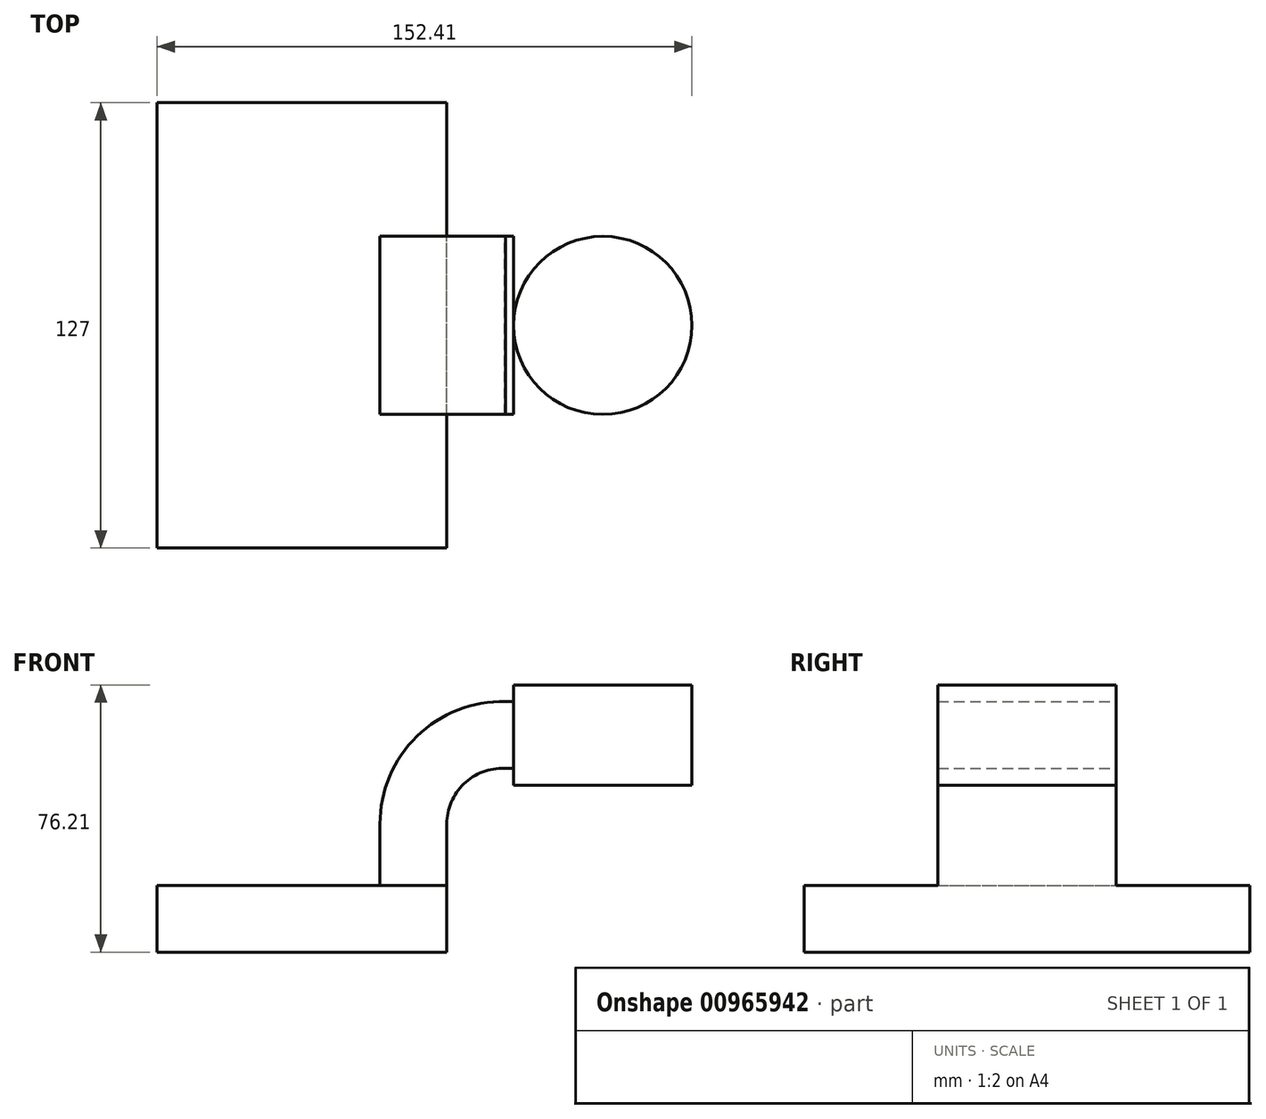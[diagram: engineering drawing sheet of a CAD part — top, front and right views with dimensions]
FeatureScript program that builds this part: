
annotation { "Feature Type Name" : "Feature", "Feature Type Description" : "" }
export const myFeature = defineFeature(function(context is Context, id is Id, definition is map)
    precondition{}
    {
        {
            var Q0;
            Q0=qCreatedBy(makeId("Front.planeOp"),FACE);
            var sketch = newSketch(context, id + "F0", { "sketchPlane" : qUnion([Q0])});
            skLineSegment(sketch, "E0.bottom", {"start": v(-41.28, 9.52) * mm, "end": v(41.28, 9.53) * mm});
            skLineSegment(sketch, "E0.top", {"start": v(-41.28, -9.53) * mm, "end": v(41.28, -9.53) * mm});
            skLineSegment(sketch, "E0.left", {"start": v(-41.28, 9.52) * mm, "end": v(-41.27, -9.53) * mm});
            skLineSegment(sketch, "E0.right", {"start": v(41.28, 9.53) * mm, "end": v(41.28, -9.52) * mm});
            skPoint(sketch, "E0.middle", {"position": v(0, 0) * mm});
            skLineSegment(sketch, "E1.bottom", {"start": v(60.32, 66.67) * mm, "end": v(111.12, 66.67) * mm});
            skLineSegment(sketch, "E1.top", {"start": v(60.32, 38.1) * mm, "end": v(111.12, 38.1) * mm});
            skLineSegment(sketch, "E1.left", {"start": v(60.32, 66.67) * mm, "end": v(60.32, 38.1) * mm});
            skLineSegment(sketch, "E1.right", {"start": v(111.12, 66.67) * mm, "end": v(111.12, 38.1) * mm});
            skPoint(sketch, "E1.middle", {"position": v(85.72, 52.39) * mm});
            skLineSegment(sketch, "E2", {"start": v(41.27, 9.53) * mm, "end": v(41.27, 27.01) * mm});
            skArc(sketch, "E3", {"start": v(41.27, 27.01) * mm, "mid": v(46.14, 38.44) * mm, "end": v(57.74, 42.88) * mm});
            skLineSegment(sketch, "E4", {"start": v(57.74, 42.88) * mm, "end": v(85.72, 42.88) * mm});
            skLineSegment(sketch, "E5.0", {"start": v(58.03, 61.93) * mm, "end": v(85.72, 61.93) * mm});
            skArc(sketch, "E5.1", {"start": v(22.22, 27.01) * mm, "mid": v(32.77, 52.02) * mm, "end": v(58.03, 61.93) * mm});
            skLineSegment(sketch, "E5.2", {"start": v(22.23, 9.53) * mm, "end": v(22.23, 27.01) * mm});
            skLineSegment(sketch, "E6", {"start": v(85.72, 38.1) * mm, "end": v(85.72, 66.67) * mm});
            skFitSpline(sketch, "E7", {"points": [v(58.03, 61.93) * mm, v(-41.28, 9.53) * mm], "startDerivative": vector(-139, 5.06) * mm, "endDerivative": vector(-16.06, -119.7) * mm});
            skSolve(sketch);
        }
        {
            var Q0;
            Q0=makeQuery(id+"F0.imprint","IMPRINT",FACE,{"disambiguationData":[TD([[makeQuery(id+"F0.imprint","IMPRINT",EDGE,{"derivedFrom":sQuery(id+"F0.wireOp",EDGE,"E0.top")}),1.0]])]});
            extrude(context, id + "F1", {"entities" : qUnion([Q0]), "endBound" : BoundingType.SYMMETRIC, "depth" : 127 * mm, "offsetDistance" : 25.4 * mm});
        }
        {
            var Q0;
            {var subQ1=sQuery(id+"F0.wireOp",EDGE,"E2");Q0=makeQuery(id+"F0.imprint","IMPRINT",FACE,{"disambiguationData":[TD([[makeQuery(id+"F0.imprint","IMPRINT",EDGE,{"derivedFrom":subQ1}),1.0]])]});}
            var Q1;
            Q1=sQuery(id+"F0.wireOp",EDGE,"E5.1");
            var Q2;
            Q2=sQuery(id+"F0.wireOp",EDGE,"E5.2");
            var Q3;
            Q3=sQuery(id+"F0.wireOp",EDGE,"E2");
            var Q4;
            Q4=sQuery(id+"F0.wireOp",EDGE,"E3");
            extrude(context, id + "F2", {"entities" : qUnion([Q0]), "operationType" : NewBodyOperationType.ADD, "surfaceEntities" : qUnion([Q1, Q2, Q3, Q4]), "endBound" : BoundingType.SYMMETRIC, "depth" : 50.8 * mm, "offsetDistance" : 25.4 * mm});
        }
        {
            var Q0;
            Q0=makeQuery(id+"F0.imprint","IMPRINT",FACE,{"disambiguationData":[TD([[makeQuery(id+"F0.imprint","IMPRINT",EDGE,{"derivedFrom":sQuery(id+"F0.wireOp",EDGE,"E5.1")}),1.0]])]});
            extrude(context, id + "F3", {"entities" : qUnion([Q0]), "operationType" : NewBodyOperationType.ADD, "endBound" : BoundingType.SYMMETRIC, "depth" : 16.5 * mm, "offsetDistance" : 25.4 * mm});
        }
        {
            var Q0;
            {var subQ0=sQuery(id+"F0.wireOp",EDGE,"E1.right");Q0=makeQuery(id+"F0.imprint","IMPRINT",FACE,{"disambiguationData":[TD([[makeQuery(id+"F0.imprint","IMPRINT",EDGE,{"derivedFrom":subQ0}),-1.0]])]});}
            var Q1;
            Q1=sQuery(id+"F0.wireOp",EDGE,"E6");
            revolve(context, id + "F4", {"operationType" : NewBodyOperationType.ADD, "surfaceOperationType" : NewSurfaceOperationType.NEW, "entities" : qUnion([Q0]), "axis" : qUnion([Q1]), "revolveType" : RevolveType.FULL});
        }
    });
